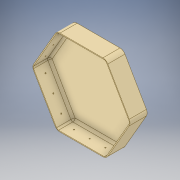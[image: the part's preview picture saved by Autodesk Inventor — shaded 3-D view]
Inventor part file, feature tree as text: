
AUTODESK INVENTOR PART (.ipt)
format: ipt  version: 2019 (Build 230136000, 136)  size: 189,952 bytes
history: native  units: mm
features: mirror x4, plane x3, extrude x2, sketch x2, fillet x2, shell x1, projected_geometry x1
ambient origin geometry x8: Origin, YZ Plane, XZ Plane, XY Plane, X Axis, Y Axis, Z Axis, Center Point
bodies: Solid1 (feature_tree)
feature tree (15):
  extrude  "Extrusion1"  Depth=30.0mm TaperAngle=0.0deg
  shell  "Shell1"  Thickness=1.5mm
  sketch  "Sketch2"  dims[d5=2.0mm d6=15.0mm d7=15.0mm d8=1.0mm d9=0.0mm d10=4.0mm d11=10.0mm d12=1.0mm]
  plane  "Work Plane1"
  plane  "Work Plane2"
  plane  "Work Plane3"
  extrude  "Extrusion2"  Depth=1.0mm
  mirror  "Mirror1"
  mirror  "Mirror2"
  mirror  "Mirror3"
  mirror  "Mirror4"
  fillet  "Fillet1"  Radius=15.0mm
  fillet  "Fillet2"  Radius=1.0mm
  sketch  "Sketch1"  dims[d0=150.0mm d2=30.0mm d3=0.0mm d4=1.5mm]
  projected_geometry  "Projected Loop1"
